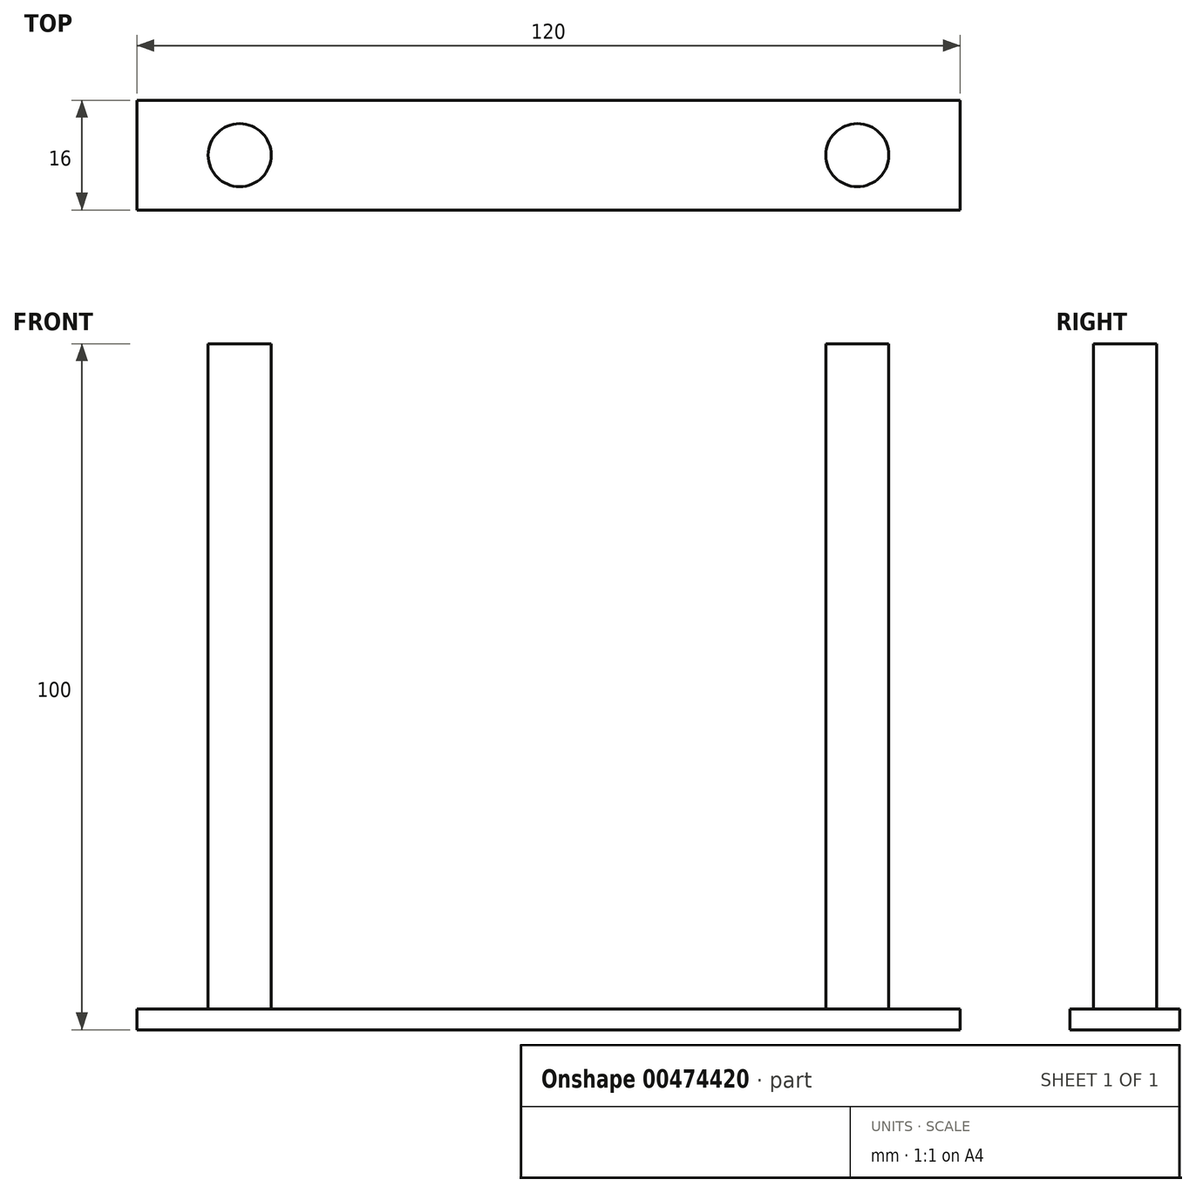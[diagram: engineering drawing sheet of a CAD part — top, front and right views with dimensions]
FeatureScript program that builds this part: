
annotation { "Feature Type Name" : "Feature", "Feature Type Description" : "" }
export const myFeature = defineFeature(function(context is Context, id is Id, definition is map)
    precondition{}
    {
        {
            var Q0;
            Q0=qCreatedBy(makeId("Top.planeOp"),FACE);
            var sketch = newSketch(context, id + "F0", { "sketchPlane" : qUnion([Q0])});
            skLineSegment(sketch, "E0.bottom", {"start": v(-60, 8) * mm, "end": v(60, 8) * mm});
            skLineSegment(sketch, "E0.top", {"start": v(-60, -8) * mm, "end": v(60, -8) * mm});
            skLineSegment(sketch, "E0.left", {"start": v(-60, 8) * mm, "end": v(-60, -8) * mm});
            skLineSegment(sketch, "E0.right", {"start": v(60, 8) * mm, "end": v(60, -8) * mm});
            skSolve(sketch);
        }
        {
            var Q0;
            Q0 = qSketchRegion(id + "F0", true);
            extrude(context, id + "F1", {"entities" : qUnion([Q0]), "depth" : 3 * mm, "offsetDistance" : 25 * mm});
        }
        {
            var Q0;
            Q0=qCreatedBy(makeId("Top.planeOp"),FACE);
            var sketch = newSketch(context, id + "F2", { "sketchPlane" : qUnion([Q0])});
            skCircle(sketch, "E1", {"center": v(-45, 0) * mm, "radius": 4.6 * mm});
            skCircle(sketch, "E2", {"center": v(45, 0) * mm, "radius": 4.6 * mm});
            skSolve(sketch);
        }
        {
            var Q0;
            Q0 = qSketchRegion(id + "F2", true);
            extrude(context, id + "F3", {"entities" : qUnion([Q0]), "operationType" : NewBodyOperationType.ADD, "depth" : 100 * mm, "offsetDistance" : 25 * mm});
        }
    });
